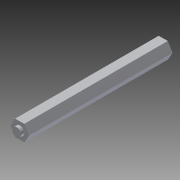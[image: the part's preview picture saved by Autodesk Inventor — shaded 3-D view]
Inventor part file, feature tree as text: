
AUTODESK INVENTOR PART (.ipt)
format: ipt  version: 2014 SP1 (Build 180222100, 222)  size: 95,744 bytes
history: native  units: in
note: dims shown in document units (in); Inventor stores cm internally (conversion verified against a paired STEP export)
features: extrude x4, sketch x4
ambient origin geometry x8: Origin, YZ Plane, XZ Plane, XY Plane, X Axis, Y Axis, Z Axis, Center Point
bodies: Solid1 (feature_tree)
feature tree (8):
  extrude  "Extrusion1"  Depth=0.5in TaperAngle=0.0deg
  extrude  "Extrusion2"  Depth=0.5in TaperAngle=0.0deg
  extrude  "Extrusion3"  [1 undecoded]
  extrude  "Extrusion4"  [1 undecoded]
  sketch  "Sketch1"  dims[d0=0.5in d1=4.0in d2=0.0in]
  sketch  "Sketch2"  dims[d3=0.01in d4=0.0in d5=0.5in d6=0.0in]
  sketch  "Sketch3"  dims[d7=0.1in d8=0.0in]
  sketch  "Sketch4"
note: 2 required parameter values undecoded (feature->parameter linkage not recoverable at this tier; creation-order binding heuristic only, values carry confidence <= 0.55)
